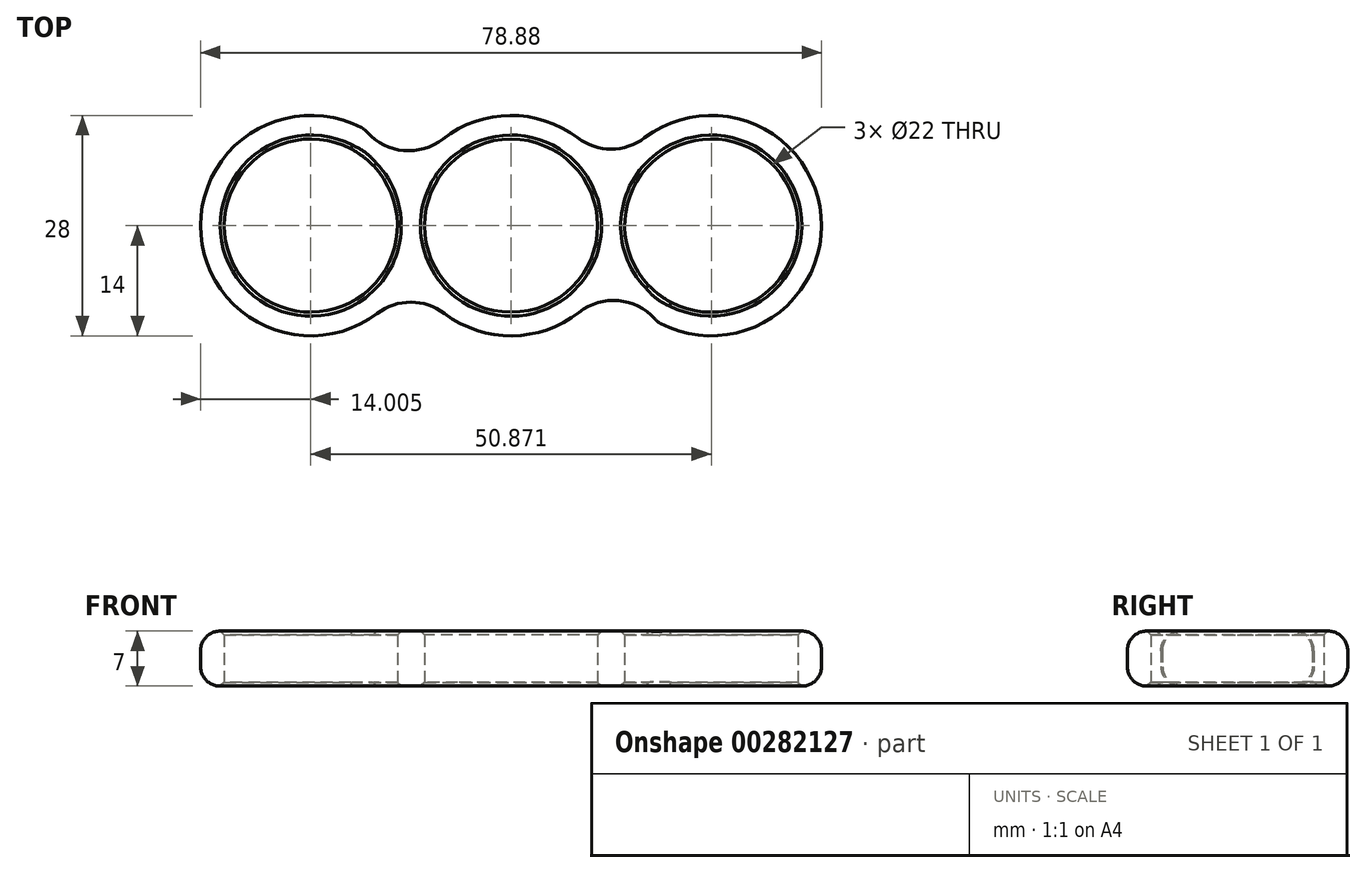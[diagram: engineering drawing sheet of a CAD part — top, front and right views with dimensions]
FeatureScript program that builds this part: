
annotation { "Feature Type Name" : "Feature", "Feature Type Description" : "" }
export const myFeature = defineFeature(function(context is Context, id is Id, definition is map)
    precondition{}
    {
        {
            var Q0;
            Q0=qCreatedBy(makeId("Top.planeOp"),FACE);
            var sketch = newSketch(context, id + "F0", { "sketchPlane" : qUnion([Q0])});
            skCircle(sketch, "E0", {"center": v(0, 0) * mm, "radius": 11 * mm});
            skCircle(sketch, "E1", {"center": v(0, 0) * mm, "radius": 14 * mm});
            skCircle(sketch, "E2", {"center": v(25.44, 0) * mm, "radius": 14 * mm});
            skArc(sketch, "E3", {"start": v(18.93, 13.42) * mm, "mid": v(12.38, 9.74) * mm, "end": v(6.21, 14.03) * mm});
            skArc(sketch, "E4.MirrorCS", {"start": v(19.21, -13.2) * mm, "mid": v(12.66, -9.52) * mm, "end": v(6.5, -13.81) * mm});
            skLineSegment(sketch, "E5", {"start": v(0, 0) * mm, "end": v(20, 0) * mm, "construction": true});
            skCircle(sketch, "E6", {"center": v(25.44, 0) * mm, "radius": 11 * mm});
            skSolve(sketch);
        }
        {
            var Q0;
            Q0=makeQuery(id+"F0.imprint","IMPRINT",FACE,{"disambiguationData":[TD([[makeQuery(id+"F0.imprint","IMPRINT",EDGE,{"derivedFrom":sQuery(id+"F0.wireOp",EDGE,"E0")}),-1.0]])]});
            var Q1;
            {var subQ0=sQuery(id+"F0.wireOp",EDGE,"E2");var subQ1=sQuery(id+"F0.wireOp",EDGE,"E1");var subQ2=makeQuery(id+"F0.imprint","INTERSECT",VERTEX,{"disambiguationData":[OD(0.0)],"derivedFrom":[subQ1,subQ0]});Q1=makeQuery(id+"F0.imprint","IMPRINT",FACE,{"disambiguationData":[TD([[makeQuery(id+"F0.imprint","IMPRINT",EDGE,{"disambiguationData":[TD([[subQ2,1.0]])],"derivedFrom":subQ1}),1.0]])]});}
            var Q2;
            Q2=makeQuery(id+"F0.imprint","IMPRINT",FACE,{"disambiguationData":[TD([[makeQuery(id+"F0.imprint","IMPRINT",EDGE,{"derivedFrom":sQuery(id+"F0.wireOp",EDGE,"c63c306a-441a-4f94-9b86-962233378e3f.1")}),1.0]])]});
            var Q3;
            {var subQ0=sQuery(id+"F0.wireOp",EDGE,"E4.MirrorCS");var subQ1=sQuery(id+"F0.wireOp",EDGE,"E1");var subQ2=makeQuery(id+"F0.imprint","INTERSECT",VERTEX,{"derivedFrom":[subQ1,subQ0]});Q3=makeQuery(id+"F0.imprint","IMPRINT",FACE,{"disambiguationData":[TD([[makeQuery(id+"F0.imprint","IMPRINT",EDGE,{"disambiguationData":[TD([[subQ2,-1.0]])],"derivedFrom":subQ1}),-1.0]])]});}
            var Q4;
            {var subQ0=sQuery(id+"F0.wireOp",EDGE,"E3");var subQ1=sQuery(id+"F0.wireOp",EDGE,"E1");var subQ2=makeQuery(id+"F0.imprint","INTERSECT",VERTEX,{"derivedFrom":[subQ1,subQ0]});Q4=makeQuery(id+"F0.imprint","IMPRINT",FACE,{"disambiguationData":[TD([[makeQuery(id+"F0.imprint","IMPRINT",EDGE,{"disambiguationData":[TD([[subQ2,1.0]])],"derivedFrom":subQ1}),-1.0]])]});}
            var Q5;
            Q5=makeQuery(id+"F0.imprint","IMPRINT",FACE,{"disambiguationData":[TD([[makeQuery(id+"F0.imprint","IMPRINT",EDGE,{"derivedFrom":sQuery(id+"F0.wireOp",EDGE,"E6")}),-1.0]])]});
            extrude(context, id + "F1", {"entities" : qUnion([Q0, Q1, Q2, Q3, Q4, Q5]), "endBound" : BoundingType.SYMMETRIC, "depth" : 7 * mm});
        }
        {
            var Q0;
            {var subQ0=sQuery(id+"F0.wireOp",EDGE,"E3");var subQ1=sQuery(id+"F0.wireOp",EDGE,"E1");var subQ2=makeQuery(id+"F0.imprint","INTERSECT",VERTEX,{"derivedFrom":[subQ1,subQ0]});Q0=makeQuery(id+"F0.imprint","IMPRINT",FACE,{"disambiguationData":[TD([[makeQuery(id+"F0.imprint","IMPRINT",EDGE,{"disambiguationData":[TD([[subQ2,1.0]])],"derivedFrom":subQ1}),-1.0]])]});}
            var Q1;
            Q1=makeQuery(id+"F0.imprint","IMPRINT",FACE,{"disambiguationData":[TD([[makeQuery(id+"F0.imprint","IMPRINT",EDGE,{"derivedFrom":sQuery(id+"F0.wireOp",EDGE,"UwXqT0ap-12Z3-Fupx-mhf0-3pL9q4EJ6cQW")}),-1.0]])]});
            var Q2;
            {var subQ0=sQuery(id+"F0.wireOp",EDGE,"gSAZEsJJ-cn3l-cjJ6-9HDa-52uPBN5IA6vx");Q2=makeQuery(id+"F0.imprint","IMPRINT",FACE,{"disambiguationData":[TD([[makeQuery(id+"F0.imprint","IMPRINT",EDGE,{"derivedFrom":subQ0}),1.0]])]});}
            var Q3;
            {var subQ0=sQuery(id+"F0.wireOp",EDGE,"VPdpeA7V-GjOX-LRlJ-2Vj8-VplDRYYToLq0");Q3=makeQuery(id+"F0.imprint","IMPRINT",FACE,{"disambiguationData":[TD([[makeQuery(id+"F0.imprint","IMPRINT",EDGE,{"derivedFrom":subQ0}),1.0]])]});}
            var Q4;
            {var subQ0=sQuery(id+"F0.wireOp",EDGE,"f63044cd-322f-4f96-b824-94d15fe920c80.MirrorCS");Q4=makeQuery(id+"F0.imprint","IMPRINT",FACE,{"disambiguationData":[TD([[makeQuery(id+"F0.imprint","IMPRINT",EDGE,{"derivedFrom":subQ0}),-1.0]])]});}
            var Q5;
            {var subQ0=sQuery(id+"F0.wireOp",EDGE,"f037a777-31d1-4705-85f1-b677b52131420.MirrorCS");Q5=makeQuery(id+"F0.imprint","IMPRINT",FACE,{"disambiguationData":[TD([[makeQuery(id+"F0.imprint","IMPRINT",EDGE,{"derivedFrom":subQ0}),-1.0]])]});}
            var Q6;
            {var subQ0=sQuery(id+"F0.wireOp",EDGE,"a2668e3b-8a0b-417b-9202-db38daa61a800.MirrorCS");Q6=makeQuery(id+"F0.imprint","IMPRINT",FACE,{"disambiguationData":[TD([[makeQuery(id+"F0.imprint","IMPRINT",EDGE,{"derivedFrom":subQ0}),-1.0]])]});}
            var Q7;
            {var subQ0=sQuery(id+"F0.wireOp",EDGE,"diWcMJ20-Xh2n-FcUL-icb3-4419BL6dKp2H");Q7=makeQuery(id+"F0.imprint","IMPRINT",FACE,{"disambiguationData":[TD([[makeQuery(id+"F0.imprint","IMPRINT",EDGE,{"derivedFrom":subQ0}),1.0]])]});}
            var Q8;
            {var subQ0=sQuery(id+"F0.wireOp",EDGE,"E4.MirrorCS");var subQ1=sQuery(id+"F0.wireOp",EDGE,"E1");var subQ2=makeQuery(id+"F0.imprint","INTERSECT",VERTEX,{"derivedFrom":[subQ1,subQ0]});Q8=makeQuery(id+"F0.imprint","IMPRINT",FACE,{"disambiguationData":[TD([[makeQuery(id+"F0.imprint","IMPRINT",EDGE,{"disambiguationData":[TD([[subQ2,-1.0]])],"derivedFrom":subQ1}),-1.0]])]});}
            extrude(context, id + "F2", {"entities" : qUnion([Q0, Q1, Q2, Q3, Q4, Q5, Q6, Q7, Q8]), "operationType" : NewBodyOperationType.ADD, "endBound" : BoundingType.SYMMETRIC, "depth" : 7 * mm});
        }
        {
            var Q0;
            Q0=makeQuery(id+"F1.opExtrude","SWEPT_FACE",FACE,{"disambiguationData":[OSD([sQuery(id+"F0.wireOp",EDGE,"E2")])]});
            fillet(context, id + "F3", {"entities" : qUnion([Q0]), "radius" : 2.5 * mm, "tangentPropagation" : true, "allowEdgeOverflow" : false});
        }
        {
            var Q0;
            Q0=makeQuery(id+"F1.opExtrude","SWEPT_FACE",FACE,{"disambiguationData":[OSD([sQuery(id+"F0.wireOp",EDGE,"E0")])]});
            var Q1;
            Q1=makeQuery(id+"F1.opExtrude","CAP_EDGE",EDGE,{"disambiguationData":[OSD([sQuery(id+"F0.wireOp",EDGE,"53f2b73f-ce0e-432c-9218-abeb8c07c58c.3")])],"isStart":false});
            var Q2;
            Q2=makeQuery(id+"F1.opExtrude","CAP_EDGE",EDGE,{"disambiguationData":[OSD([sQuery(id+"F0.wireOp",EDGE,"53f2b73f-ce0e-432c-9218-abeb8c07c58c.4")])],"isStart":false});
            var Q3;
            Q3=makeQuery(id+"F1.opExtrude","CAP_EDGE",EDGE,{"disambiguationData":[OSD([sQuery(id+"F0.wireOp",EDGE,"c63c306a-441a-4f94-9b86-962233378e3f.1")])],"isStart":false});
            var Q4;
            Q4=makeQuery(id+"F1.opExtrude","CAP_EDGE",EDGE,{"disambiguationData":[OSD([sQuery(id+"F0.wireOp",EDGE,"c63c306a-441a-4f94-9b86-962233378e3f.2")])],"isStart":false});
            var Q5;
            {var subQ0=sQuery(id+"F0.wireOp",EDGE,"E2");var subQ1=makeQuery(id+"F0.imprint","INTERSECT",VERTEX,{"derivedFrom":[subQ0,sQuery(id+"F0.wireOp",EDGE,"E3")]});Q5=makeQuery(id+"F3.opFillet","BLEND_EDGE",EDGE,{"blendedFrom":[makeQuery(id+"F1.opExtrude","CAP_EDGE",EDGE,{"disambiguationData":[OSD([subQ0]),TDD([makeQuery(id+"F0.imprint","IMPRINT",EDGE,{"disambiguationData":[TD([[subQ1,-1.0]])],"derivedFrom":subQ0}),makeQuery(id+"F0.imprint","IMPRINT",EDGE,{"disambiguationData":[TD([[subQ1,1.0]])],"derivedFrom":subQ0})])],"isStart":false}),makeQuery(id+"F1.opExtrude","SWEPT_FACE",FACE,{"disambiguationData":[OSD([sQuery(id+"F0.wireOp",EDGE,"c63c306a-441a-4f94-9b86-962233378e3f.3")])]})],"blendedInto":[makeQuery(id+"F1.opExtrude","SWEPT_FACE",FACE,{"disambiguationData":[OSD([sQuery(id+"F0.wireOp",EDGE,"c63c306a-441a-4f94-9b86-962233378e3f.3")])]})]});}
            var Q6;
            Q6=makeQuery(id+"F1.opExtrude","CAP_EDGE",EDGE,{"disambiguationData":[OSD([sQuery(id+"F0.wireOp",EDGE,"c63c306a-441a-4f94-9b86-962233378e3f.4")])],"isStart":false});
            var Q7;
            Q7=makeQuery(id+"F1.opExtrude","CAP_EDGE",EDGE,{"disambiguationData":[OSD([sQuery(id+"F0.wireOp",EDGE,"c63c306a-441a-4f94-9b86-962233378e3f.5")])],"isStart":false});
            var Q8;
            Q8=makeQuery(id+"F1.opExtrude","CAP_EDGE",EDGE,{"disambiguationData":[OSD([sQuery(id+"F0.wireOp",EDGE,"53f2b73f-ce0e-432c-9218-abeb8c07c58c.0")])],"isStart":false});
            var Q9;
            Q9=makeQuery(id+"F1.opExtrude","CAP_EDGE",EDGE,{"disambiguationData":[OSD([sQuery(id+"F0.wireOp",EDGE,"53f2b73f-ce0e-432c-9218-abeb8c07c58c.1")])],"isStart":false});
            var Q10;
            Q10=makeQuery(id+"F1.opExtrude","CAP_EDGE",EDGE,{"disambiguationData":[OSD([sQuery(id+"F0.wireOp",EDGE,"53f2b73f-ce0e-432c-9218-abeb8c07c58c.2")])],"isStart":false});
            var Q11;
            Q11=makeQuery(id+"F1.opExtrude","CAP_EDGE",EDGE,{"disambiguationData":[OSD([sQuery(id+"F0.wireOp",EDGE,"c63c306a-441a-4f94-9b86-962233378e3f.1")])],"isStart":true});
            var Q12;
            Q12=makeQuery(id+"F1.opExtrude","SWEPT_FACE",FACE,{"disambiguationData":[OSD([sQuery(id+"F0.wireOp",EDGE,"c63c306a-441a-4f94-9b86-962233378e3f.2")])]});
            var Q13;
            Q13=makeQuery(id+"F1.opExtrude","SWEPT_FACE",FACE,{"disambiguationData":[OSD([sQuery(id+"F0.wireOp",EDGE,"c63c306a-441a-4f94-9b86-962233378e3f.4")])]});
            var Q14;
            Q14=makeQuery(id+"F1.opExtrude","SWEPT_FACE",FACE,{"disambiguationData":[OSD([sQuery(id+"F0.wireOp",EDGE,"53f2b73f-ce0e-432c-9218-abeb8c07c58c.0")])]});
            var Q15;
            Q15=makeQuery(id+"F1.opExtrude","SWEPT_FACE",FACE,{"disambiguationData":[OSD([sQuery(id+"F0.wireOp",EDGE,"53f2b73f-ce0e-432c-9218-abeb8c07c58c.1")])]});
            var Q16;
            Q16=makeQuery(id+"F1.opExtrude","SWEPT_FACE",FACE,{"disambiguationData":[OSD([sQuery(id+"F0.wireOp",EDGE,"53f2b73f-ce0e-432c-9218-abeb8c07c58c.2")])]});
            var Q17;
            Q17=makeQuery(id+"F1.opExtrude","SWEPT_FACE",FACE,{"disambiguationData":[OSD([sQuery(id+"F0.wireOp",EDGE,"53f2b73f-ce0e-432c-9218-abeb8c07c58c.4")])]});
            var Q18;
            Q18=makeQuery(id+"F1.opExtrude","CAP_EDGE",EDGE,{"disambiguationData":[OSD([sQuery(id+"F0.wireOp",EDGE,"E6")])],"isStart":true});
            var Q19;
            Q19=makeQuery(id+"F1.opExtrude","CAP_EDGE",EDGE,{"disambiguationData":[OSD([sQuery(id+"F0.wireOp",EDGE,"E6")])],"isStart":false});
            chamfer(context, id + "F4", {"entities" : qUnion([Q0, Q1, Q2, Q3, Q4, Q5, Q6, Q7, Q8, Q9, Q10, Q11, Q12, Q13, Q14, Q15, Q16, Q17, Q18, Q19]), "width" : .5 * mm, "tangentPropagation" : true});
        }
        {
            var Q0;
            Q0=makeQuery(id+"F1.opExtrude","SWEPT_BODY",BODY,{"disambiguationData":[OSD([sQuery(id+"F0.wireOp",EDGE,"E0"),sQuery(id+"F0.wireOp",EDGE,"E1"),sQuery(id+"F0.wireOp",EDGE,"UwXqT0ap-12Z3-Fupx-mhf0-3pL9q4EJ6cQW"),sQuery(id+"F0.wireOp",EDGE,"E3"),sQuery(id+"F0.wireOp",EDGE,"E4.MirrorCS"),sQuery(id+"F0.wireOp",EDGE,"gSAZEsJJ-cn3l-cjJ6-9HDa-52uPBN5IA6vx"),sQuery(id+"F0.wireOp",EDGE,"VPdpeA7V-GjOX-LRlJ-2Vj8-VplDRYYToLq0"),sQuery(id+"F0.wireOp",EDGE,"diWcMJ20-Xh2n-FcUL-icb3-4419BL6dKp2H"),sQuery(id+"F0.wireOp",EDGE,"f63044cd-322f-4f96-b824-94d15fe920c80.MirrorCS"),sQuery(id+"F0.wireOp",EDGE,"f037a777-31d1-4705-85f1-b677b52131420.MirrorCS"),sQuery(id+"F0.wireOp",EDGE,"a2668e3b-8a0b-417b-9202-db38daa61a800.MirrorCS")])]});
            var Q1;
            Q1=makeQuery(id+"F1.opExtrude","SWEPT_FACE",FACE,{"disambiguationData":[OSD([sQuery(id+"F0.wireOp",EDGE,"E0")])]});
            circularPattern(context, id + "F5", {"operationType" : NewBodyOperationType.ADD, "entities" : qUnion([Q0]), "axis" : qUnion([Q1]), "angle" : 360 * degree, "instanceCount" : 2, "equalSpace" : true});
        }
    });
